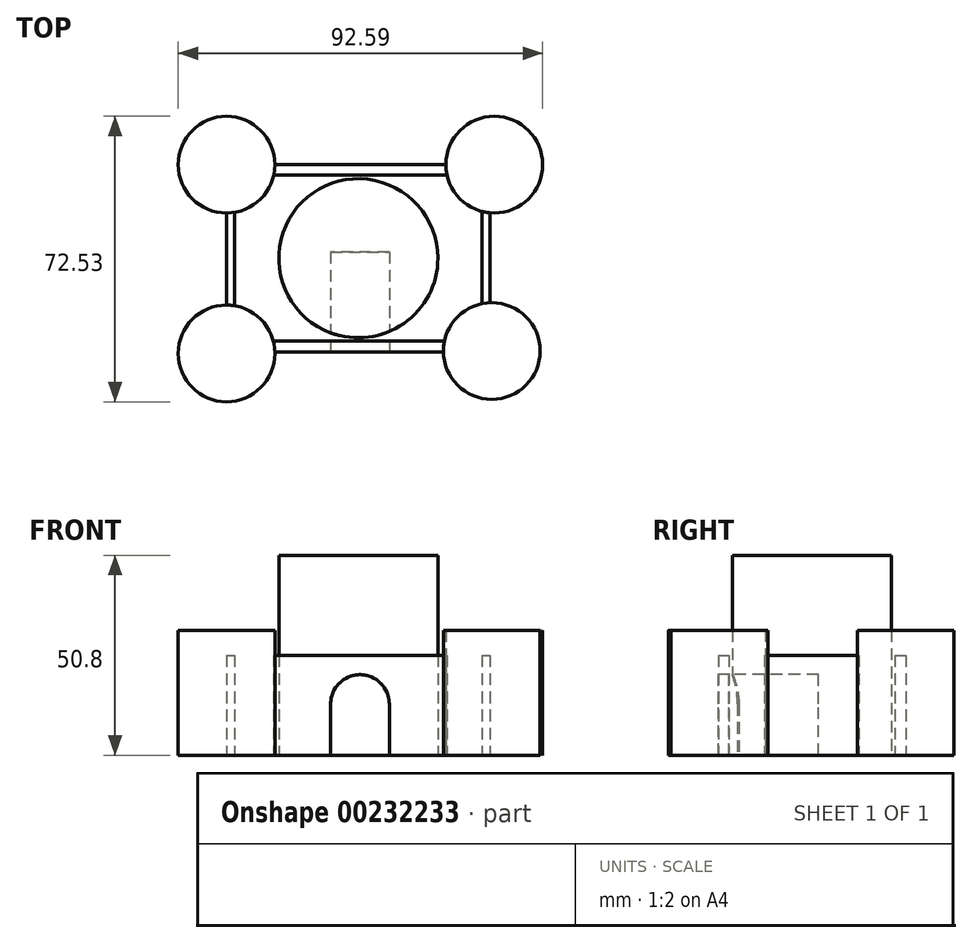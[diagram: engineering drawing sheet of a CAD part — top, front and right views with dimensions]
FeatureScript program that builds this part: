
annotation { "Feature Type Name" : "Feature", "Feature Type Description" : "" }
export const myFeature = defineFeature(function(context is Context, id is Id, definition is map)
    precondition{}
    {
        {
            var Q0;
            Q0=qCreatedBy(makeId("Top.planeOp"),FACE);
            var sketch = newSketch(context, id + "F0", { "sketchPlane" : qUnion([Q0])});
            skLineSegment(sketch, "E0.bottom", {"start": v(-21.2, 23.78) * mm, "end": v(22.24, 23.78) * mm});
            skLineSegment(sketch, "E0.top", {"start": v(-21.22, -23.78) * mm, "end": v(21.62, -23.78) * mm});
            skLineSegment(sketch, "E0.left", {"start": v(-33.5, 11.5) * mm, "end": v(-33.5, -11.9) * mm});
            skLineSegment(sketch, "E0.right", {"start": v(33.5, 11.54) * mm, "end": v(33.5, -11.3) * mm});
            skPoint(sketch, "E0.middle", {"position": v(0, 0) * mm});
            skCircle(sketch, "E1", {"center": v(0, 0) * mm, "radius": 20.2 * mm});
            skCircle(sketch, "E2", {"center": v(-33.5, 23.78) * mm, "radius": 12.28 * mm});
            skCircle(sketch, "E3", {"center": v(-33.5, -24.19) * mm, "radius": 12.28 * mm});
            skCircle(sketch, "E4", {"center": v(34.53, 23.78) * mm, "radius": 12.28 * mm});
            skCircle(sketch, "E5", {"center": v(33.9, -23.57) * mm, "radius": 12.28 * mm});
            skPoint(sketch, "E6.orphan", {"position": v(33.5, 23.78) * mm});
            skPoint(sketch, "E7.orphan", {"position": v(33.5, -23.78) * mm});
            skPoint(sketch, "E8.orphan", {"position": v(-33.5, -23.78) * mm});
            skLineSegment(sketch, "E9.bottom", {"start": v(21.88, -21.09) * mm, "end": v(-21.6, -21.09) * mm});
            skLineSegment(sketch, "E9.top", {"start": v(22.54, 21.09) * mm, "end": v(-21.5, 21.09) * mm});
            skLineSegment(sketch, "E9.left", {"start": v(31.42, -11.54) * mm, "end": v(31.42, 11.9) * mm});
            skLineSegment(sketch, "E9.right", {"start": v(-31.42, -12.08) * mm, "end": v(-31.42, 11.67) * mm});
            skPoint(sketch, "E10.orphan", {"position": v(-31.42, 21.09) * mm});
            skPoint(sketch, "E11.orphan", {"position": v(-31.42, -21.09) * mm});
            skPoint(sketch, "E12.orphan", {"position": v(31.42, -21.09) * mm});
            skPoint(sketch, "E13.orphan", {"position": v(31.42, 21.09) * mm});
            skSolve(sketch);
        }
        {
            var Q0;
            {var subQ0=sQuery(id+"F0.wireOp",EDGE,"E0.bottom");Q0=makeQuery(id+"F0.imprint","IMPRINT",FACE,{"disambiguationData":[TD([[makeQuery(id+"F0.imprint","IMPRINT",EDGE,{"derivedFrom":subQ0}),-1.0]])]});}
            var Q1;
            {var subQ0=sQuery(id+"F0.wireOp",EDGE,"E0.right");Q1=makeQuery(id+"F0.imprint","IMPRINT",FACE,{"disambiguationData":[TD([[makeQuery(id+"F0.imprint","IMPRINT",EDGE,{"derivedFrom":subQ0}),-1.0]])]});}
            var Q2;
            {var subQ0=sQuery(id+"F0.wireOp",EDGE,"E0.top");Q2=makeQuery(id+"F0.imprint","IMPRINT",FACE,{"disambiguationData":[TD([[makeQuery(id+"F0.imprint","IMPRINT",EDGE,{"derivedFrom":subQ0}),1.0]])]});}
            var Q3;
            {var subQ0=sQuery(id+"F0.wireOp",EDGE,"E0.left");Q3=makeQuery(id+"F0.imprint","IMPRINT",FACE,{"disambiguationData":[TD([[makeQuery(id+"F0.imprint","IMPRINT",EDGE,{"derivedFrom":subQ0}),1.0]])]});}
            extrude(context, id + "F1", {"entities" : qUnion([Q0, Q1, Q2, Q3]), "depth" : 25.4 * mm});
        }
        {
            var Q0;
            {var subQ0=sQuery(id+"F0.wireOp",EDGE,"E2");var subQ1=makeQuery(id+"F0.imprint","INTERSECT",VERTEX,{"derivedFrom":[sQuery(id+"F0.wireOp",EDGE,"E0.bottom"),subQ0]});Q0=makeQuery(id+"F0.imprint","IMPRINT",FACE,{"disambiguationData":[TD([[makeQuery(id+"F0.imprint","IMPRINT",EDGE,{"disambiguationData":[TD([[subQ1,-1.0]])],"derivedFrom":subQ0}),1.0]])]});}
            var Q1;
            {var subQ0=sQuery(id+"F0.wireOp",EDGE,"E3");var subQ1=makeQuery(id+"F0.imprint","INTERSECT",VERTEX,{"derivedFrom":[sQuery(id+"F0.wireOp",EDGE,"E0.top"),subQ0]});Q1=makeQuery(id+"F0.imprint","IMPRINT",FACE,{"disambiguationData":[TD([[makeQuery(id+"F0.imprint","IMPRINT",EDGE,{"disambiguationData":[TD([[subQ1,-1.0]])],"derivedFrom":subQ0}),1.0]])]});}
            var Q2;
            {var subQ0=sQuery(id+"F0.wireOp",EDGE,"E4");var subQ1=makeQuery(id+"F0.imprint","INTERSECT",VERTEX,{"derivedFrom":[sQuery(id+"F0.wireOp",EDGE,"E0.bottom"),subQ0]});Q2=makeQuery(id+"F0.imprint","IMPRINT",FACE,{"disambiguationData":[TD([[makeQuery(id+"F0.imprint","IMPRINT",EDGE,{"disambiguationData":[TD([[subQ1,-1.0]])],"derivedFrom":subQ0}),1.0]])]});}
            var Q3;
            {var subQ0=sQuery(id+"F0.wireOp",EDGE,"E5");var subQ1=makeQuery(id+"F0.imprint","INTERSECT",VERTEX,{"derivedFrom":[sQuery(id+"F0.wireOp",EDGE,"E0.right"),subQ0]});Q3=makeQuery(id+"F0.imprint","IMPRINT",FACE,{"disambiguationData":[TD([[makeQuery(id+"F0.imprint","IMPRINT",EDGE,{"disambiguationData":[TD([[subQ1,-1.0]])],"derivedFrom":subQ0}),1.0]])]});}
            extrude(context, id + "F2", {"entities" : qUnion([Q0, Q1, Q2, Q3]), "depth" : 31.75 * mm});
        }
        {
            var Q0;
            Q0=makeQuery(id+"F0.imprint","IMPRINT",FACE,{"disambiguationData":[TD([[makeQuery(id+"F0.imprint","IMPRINT",EDGE,{"derivedFrom":sQuery(id+"F0.wireOp",EDGE,"E1")}),1.0]])]});
            extrude(context, id + "F3", {"entities" : qUnion([Q0]), "depth" : 50.8 * mm});
        }
        {
            var Q0;
            Q0=makeQuery(id+"F1.opExtrude","SWEPT_FACE",FACE,{"disambiguationData":[OSD([sQuery(id+"F0.wireOp",EDGE,"E0.top")])]});
            var sketch = newSketch(context, id + "F4", { "sketchPlane" : qUnion([Q0])});
            skLineSegment(sketch, "E14.bottom", {"start": v(-7.03, 0) * mm, "end": v(7.86, 0) * mm});
            skLineSegment(sketch, "E14.left", {"start": v(-7.03, 0) * mm, "end": v(-7.03, 13.02) * mm});
            skLineSegment(sketch, "E14.right", {"start": v(7.86, 0) * mm, "end": v(7.86, 13.02) * mm});
            skArc(sketch, "E15", {"start": v(7.86, 13.02) * mm, "mid": v(0.41, 20.47) * mm, "end": v(-7.03, 13.02) * mm});
            skSolve(sketch);
        }
        {
            var Q0;
            Q0=makeQuery(id+"F4.imprint","IMPRINT",FACE,{"disambiguationData":[TD([[makeQuery(id+"F4.imprint","IMPRINT",EDGE,{"derivedFrom":sQuery(id+"F4.wireOp",EDGE,"E14.bottom")}),1.0]])]});
            extrude(context, id + "F5", {"entities" : qUnion([Q0]), "operationType" : NewBodyOperationType.REMOVE, "oppositeDirection" : true, "depth" : 25.4 * mm});
        }
    });
